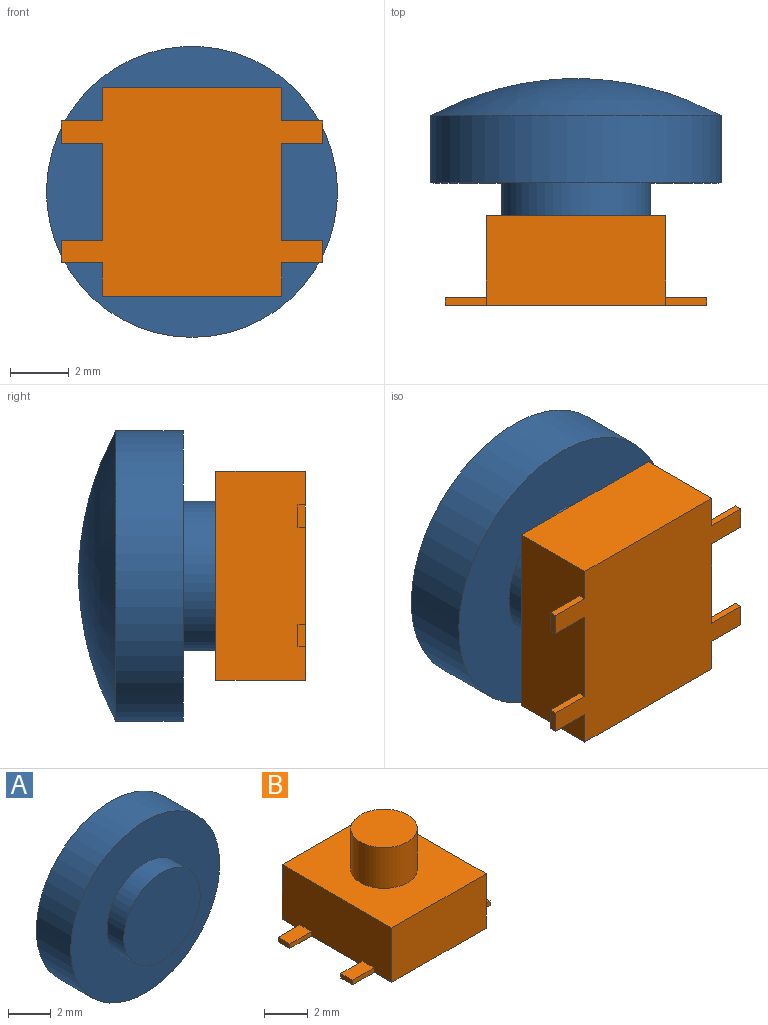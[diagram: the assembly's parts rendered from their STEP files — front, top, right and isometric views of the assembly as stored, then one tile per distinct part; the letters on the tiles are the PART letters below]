
ASSEMBLY  parts=2 mates=1
PART A: 5 faces, bbox 9.9x4.7x9.9 mm
  f0: revolved ~9.91x9.91mm, area 82mm2, adj f1
  f1: cylinder r=4.95mm len=9.91mm, axis (0,-1,0), area 71.1mm2, adj f0,f2
  f2: plane 9.91x9.91mm, normal (0,-1,0), area 56.8mm2, adj f1,f3
  f3: cylinder r=2.54mm len=5.08mm, axis (0,-1,0), area 17.8mm2, adj f2,f4
  f4: plane 5.08x5.08mm, normal (0,-1,0), area 20.3mm2, adj f3
PART B: 24 faces, bbox 8.9x7.1x5.3 mm
  f0: plane 1.41x0.25mm, normal (0,1,0), area 0.4mm2, adj f1,f3,f4,f18
  f1: plane 0.76x0.25mm, normal (-1,0,0), area 0.2mm2, adj f0,f2,f3,f4
  f2: plane 1.41x0.25mm, normal (0,-1,0), area 0.4mm2, adj f1,f3,f4,f18
  f3: plane 1.41x0.76mm, normal (0,0,1), area 1.1mm2, adj f0,f1,f2,f18
  f4: plane 8.9x7.11mm, normal (0,0,-1), area 47.6mm2, adj f0,f1,f2,f5,f6,f7,f9,f10
  f5: plane 1.41x0.25mm, normal (0,1,0), area 0.4mm2, adj f4,f6,f8,f18
  f6: plane 0.76x0.25mm, normal (-1,0,0), area 0.2mm2, adj f4,f5,f7,f8
  f7: plane 1.41x0.25mm, normal (0,-1,0), area 0.4mm2, adj f4,f6,f8,f18
  f8: plane 1.41x0.76mm, normal (0,0,1), area 1.1mm2, adj f5,f6,f7,f18
  f9: plane 1.4x0.25mm, normal (0,1,0), area 0.4mm2, adj f4,f11,f12,f13
  f10: plane 1.4x0.25mm, normal (0,-1,0), area 0.4mm2, adj f4,f11,f12,f13
  f11: plane 0.76x0.25mm, normal (1,0,0), area 0.2mm2, adj f4,f9,f10,f12
  f12: plane 1.4x0.76mm, normal (0,0,1), area 1.1mm2, adj f9,f10,f11,f13
  f13: plane 7.11x3.05mm, normal (1,0,0), area 21.3mm2, adj f4,f9,f10,f12,f14,f15,f17,f19
  f14: plane 1.4x0.25mm, normal (0,1,0), area 0.4mm2, adj f4,f13,f16,f17
  f15: plane 1.4x0.25mm, normal (0,-1,0), area 0.4mm2, adj f4,f13,f16,f17
  f16: plane 0.76x0.25mm, normal (1,0,0), area 0.2mm2, adj f4,f14,f15,f17
  f17: plane 1.4x0.76mm, normal (0,0,1), area 1.1mm2, adj f13,f14,f15,f16
  f18: plane 7.11x3.05mm, normal (-1,0,0), area 21.3mm2, adj f0,f2,f3,f4,f5,f7,f8,f19
  f19: plane 6.1x3.05mm, normal (0,-1,0), area 18.6mm2, adj f4,f13,f18,f21
  f20: plane 6.1x3.05mm, normal (0,1,0), area 18.6mm2, adj f4,f13,f18,f21
  f21: plane 7.11x6.1mm, normal (0,0,1), area 36.1mm2, adj f13,f18,f19,f20,f22
  f22: cylinder r=1.52mm len=3.05mm, axis (0,0,-1), area 21.9mm2, adj f21,f23
  f23: plane 3.05x3.05mm, normal (0,0,1), area 7.3mm2, adj f22
PLACE A t=(0.66,-0.67,-0.72)mm
PLACE B rot(axis=(-1,0,0),90deg) t=(0.66,-4.84,-0.72)mm
MATE fastened B.f22 <-> A.f1  axis (0,1,0) through (0.66,0.5,-0.72)mm
